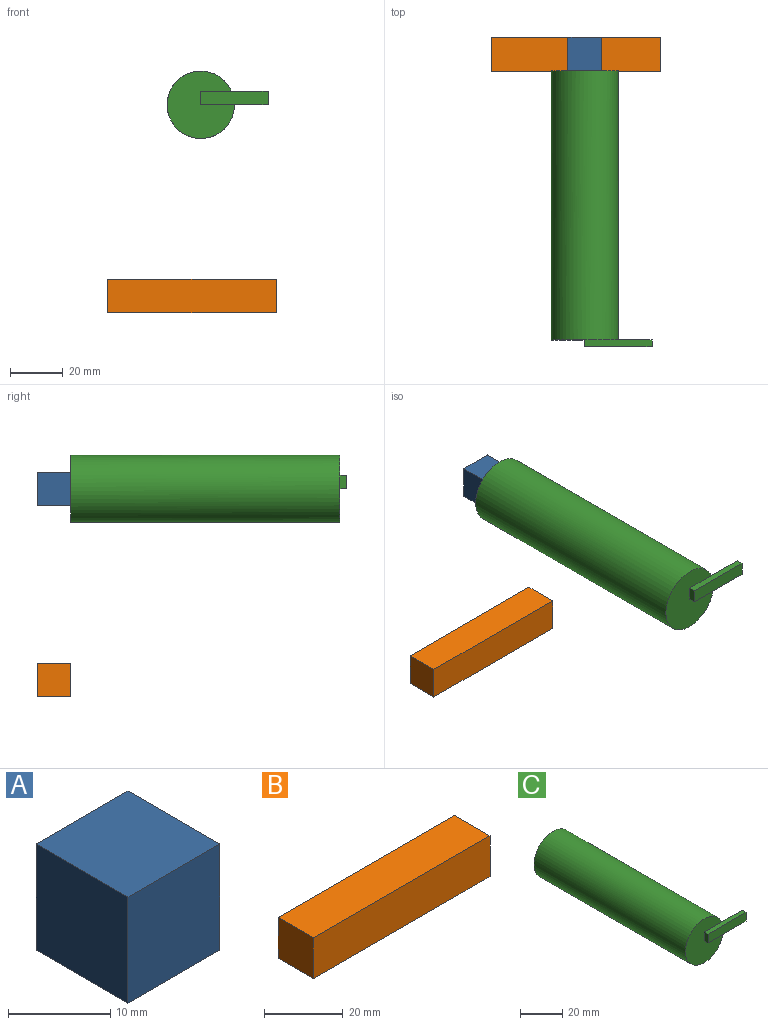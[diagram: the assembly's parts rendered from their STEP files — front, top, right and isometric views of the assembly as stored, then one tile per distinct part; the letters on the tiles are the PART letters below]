
ASSEMBLY  parts=3 mates=1
PART A: 6 faces, bbox 12.7x12.7x12.7 mm
  f0: plane 12.7x12.7mm, normal (0,0,-1), area 161.3mm2, adj f1,f3,f4,f5
  f1: plane 12.7x12.7mm, normal (1,0,0), area 161.3mm2, adj f0,f2,f4,f5
  f2: plane 12.7x12.7mm, normal (0,0,1), area 161.3mm2, adj f1,f3,f4,f5
  f3: plane 12.7x12.7mm, normal (-1,0,0), area 161.3mm2, adj f0,f2,f4,f5
  f4: plane 12.7x12.7mm, normal (0,-1,0), area 161.3mm2, adj f0,f1,f2,f3
  f5: plane 12.7x12.7mm, normal (0,1,0), area 161.3mm2, adj f0,f1,f2,f3
PART B: 6 faces, bbox 63.5x12.7x12.7 mm
  f0: plane 63.5x12.7mm, normal (0,0,-1), area 806.5mm2, adj f1,f3,f4,f5
  f1: plane 12.7x12.7mm, normal (1,0,0), area 161.3mm2, adj f0,f2,f4,f5
  f2: plane 63.5x12.7mm, normal (0,0,1), area 806.5mm2, adj f1,f3,f4,f5
  f3: plane 12.7x12.7mm, normal (-1,0,0), area 161.3mm2, adj f0,f2,f4,f5
  f4: plane 63.5x12.7mm, normal (0,-1,0), area 806.5mm2, adj f0,f1,f2,f3
  f5: plane 63.5x12.7mm, normal (0,1,0), area 806.5mm2, adj f0,f1,f2,f3
PART C: 9 faces, bbox 38.1x104.1x25.4 mm
  f0: plane 25.4x25.4mm, normal (0,-1,0), area 444mm2, adj f1,f4,f5,f6
  f1: cylinder r=12.7mm len=101.6mm, axis (0,1,0), area 8107.3mm2, adj f0,f2,f3
  f2: plane 25.4x25.4mm, normal (0,1,0), area 506.7mm2, adj f1
  f3: plane 13.76x5.08mm, normal (0,1,0), area 66.3mm2, adj f1,f4,f6,f7
  f4: plane 25.4x2.54mm, normal (0,0,1), area 64.5mm2, adj f0,f3,f5,f7,f8
  f5: plane 5.08x2.54mm, normal (-1,0,0), area 12.9mm2, adj f0,f4,f6,f8
  f6: plane 25.4x2.54mm, normal (0,0,-1), area 64.5mm2, adj f0,f3,f5,f7,f8
  f7: plane 5.08x2.54mm, normal (1,0,0), area 12.9mm2, adj f3,f4,f6,f8
  f8: plane 25.4x5.08mm, normal (0,-1,0), area 129mm2, adj f4,f5,f6,f7
PLACE A t=(-49.64,-1.32,-26.72)mm
PLACE B t=(-49.64,-1.32,-26.72)mm
PLACE C t=(-49.64,-14.02,1.86)mm
MATE planar C.f1 <-> A.f4  axis (0,1,0) through (-49.64,-14.02,1.86)mm
